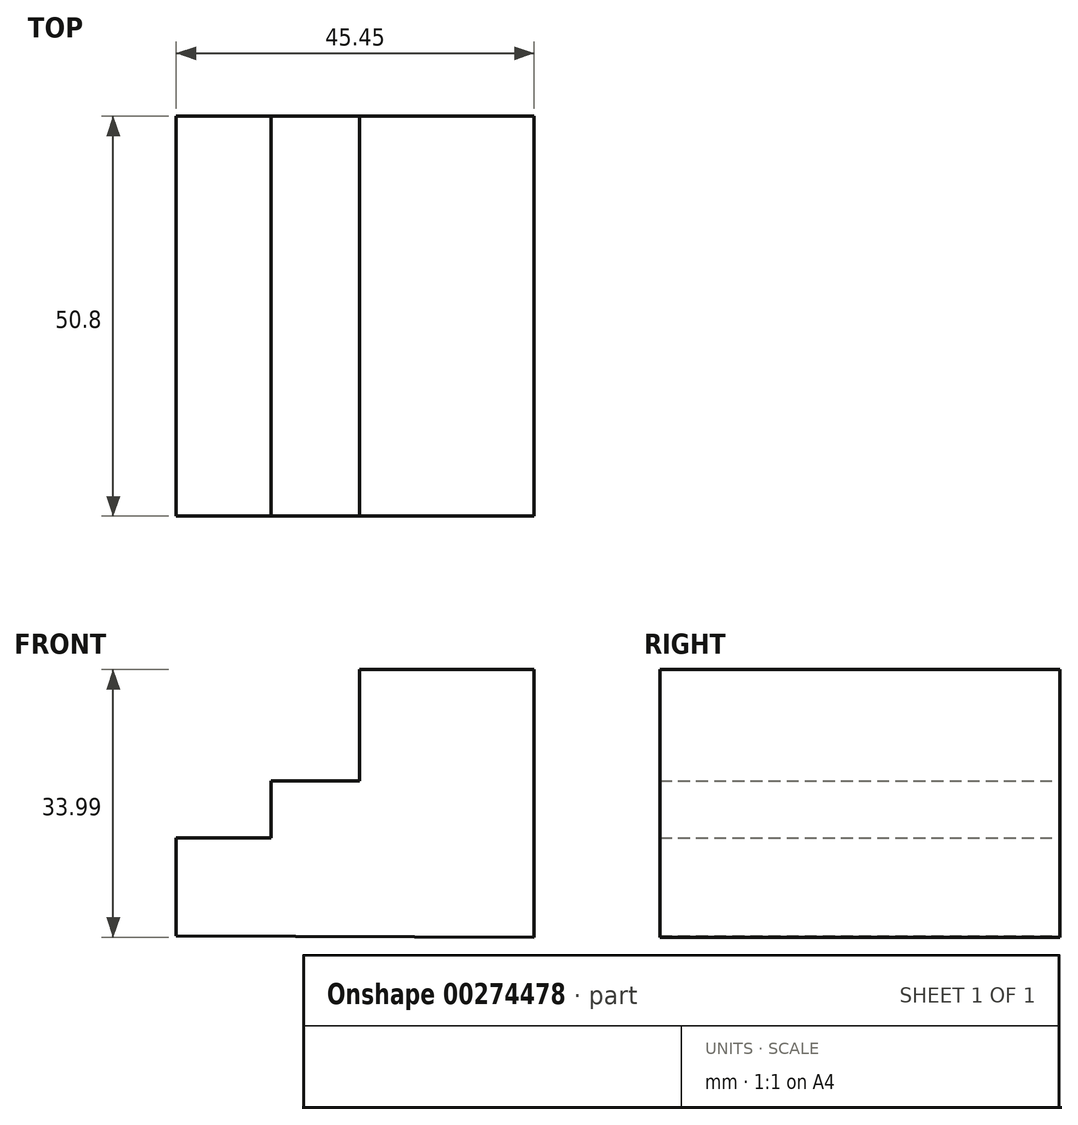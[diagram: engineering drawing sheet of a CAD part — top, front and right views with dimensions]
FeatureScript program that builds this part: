
annotation { "Feature Type Name" : "Feature", "Feature Type Description" : "" }
export const myFeature = defineFeature(function(context is Context, id is Id, definition is map)
    precondition{}
    {
        {
            var Q0;
            Q0=qCreatedBy(makeId("Front.planeOp"),FACE);
            var sketch = newSketch(context, id + "F0", { "sketchPlane" : qUnion([Q0])});
            skLineSegment(sketch, "E0", {"start": v(-55.57, 5.73) * mm, "end": v(-55.57, 18.14) * mm});
            skLineSegment(sketch, "E1", {"start": v(-55.57, 18.14) * mm, "end": v(-43.54, 18.14) * mm});
            skLineSegment(sketch, "E2", {"start": v(-43.54, 18.14) * mm, "end": v(-43.54, 25.4) * mm});
            skLineSegment(sketch, "E3", {"start": v(-43.54, 25.4) * mm, "end": v(-32.27, 25.4) * mm});
            skLineSegment(sketch, "E4", {"start": v(-32.27, 25.4) * mm, "end": v(-32.27, 39.53) * mm});
            skLineSegment(sketch, "E5", {"start": v(-32.27, 39.53) * mm, "end": v(-10.12, 39.53) * mm});
            skLineSegment(sketch, "E6", {"start": v(-10.12, 39.53) * mm, "end": v(-10.12, 5.54) * mm});
            skLineSegment(sketch, "E7", {"start": v(-10.12, 5.54) * mm, "end": v(-55.57, 5.73) * mm});
            skSolve(sketch);
        }
        {
            var Q0;
            Q0 = qSketchRegion(id + "F0", true);
            extrude(context, id + "F1", {"entities" : qUnion([Q0]), "depth" : 50.8 * mm});
        }
    });
